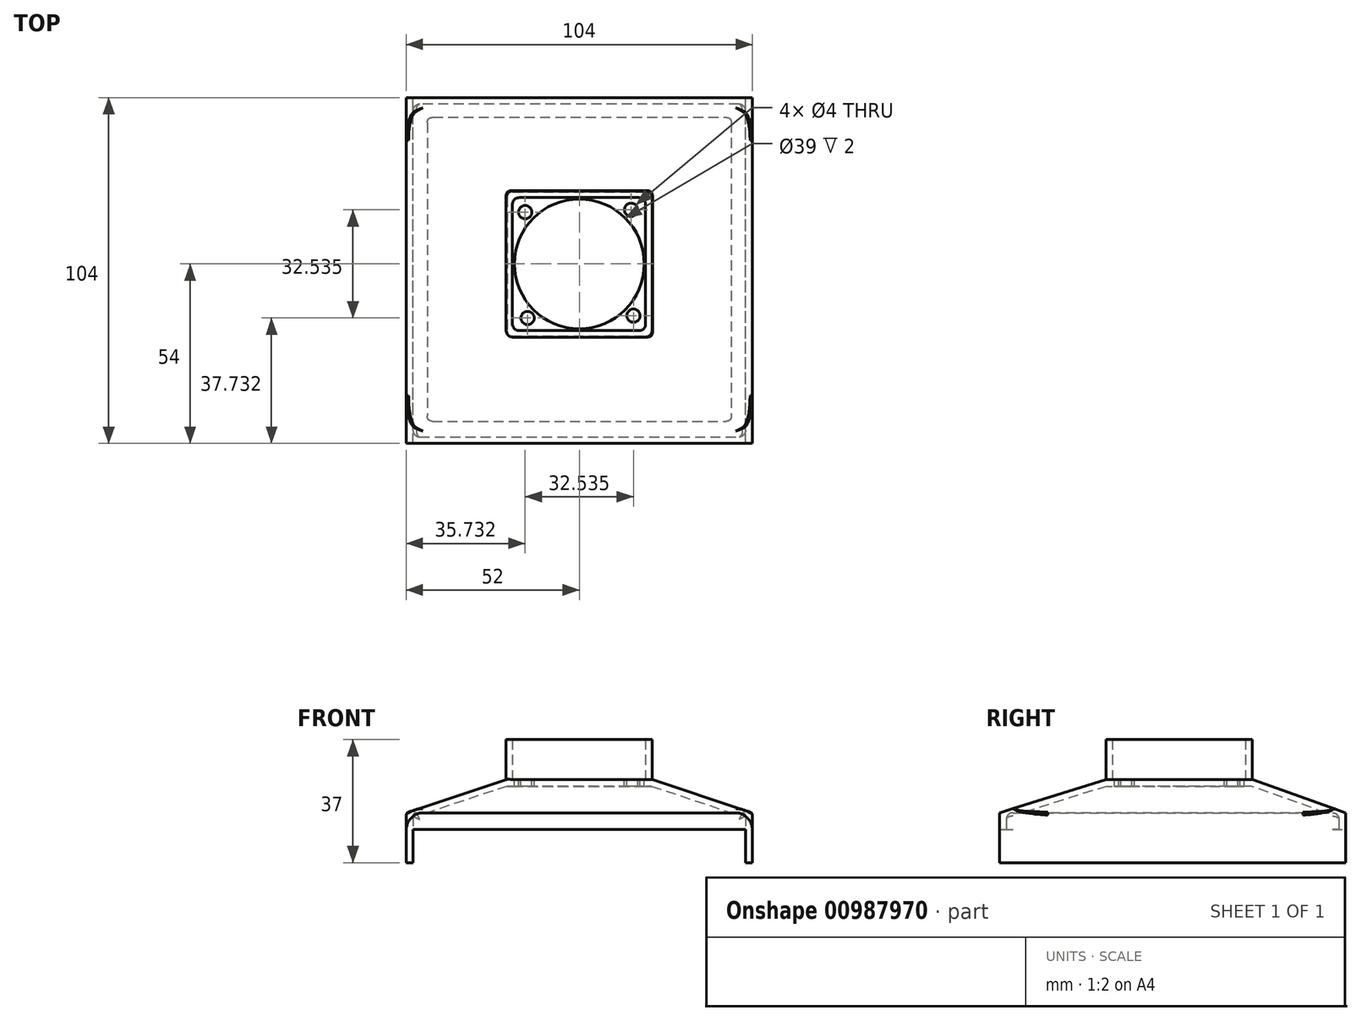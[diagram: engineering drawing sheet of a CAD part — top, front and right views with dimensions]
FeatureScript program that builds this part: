
annotation { "Feature Type Name" : "Feature", "Feature Type Description" : "" }
export const myFeature = defineFeature(function(context is Context, id is Id, definition is map)
    precondition{}
    {
        {
            var Q0;
            Q0=qCreatedBy(makeId("Top.planeOp"),FACE);
            var sketch = newSketch(context, id + "F0", { "sketchPlane" : qUnion([Q0])});
            skLineSegment(sketch, "E0.bottom", {"start": v(-52, 50) * mm, "end": v(52, 50) * mm});
            skLineSegment(sketch, "E0.top", {"start": v(-52, -54) * mm, "end": v(52, -54) * mm});
            skLineSegment(sketch, "E0.left", {"start": v(-52, 50) * mm, "end": v(-52, -54) * mm});
            skLineSegment(sketch, "E0.right", {"start": v(52, 50) * mm, "end": v(52, -54) * mm});
            skSolve(sketch);
        }
        {
            var Q0;
            Q0=qCreatedBy(makeId("Top.planeOp"),FACE);
            cPlane(context, id + "F1", {"entities" : qUnion([Q0]), "cplaneType" : CPlaneType.OFFSET, "offset" : 10 * mm, "width" : 150 * mm, "height" : 150 * mm});
        }
        {
            var Q0;
            Q0=qCreatedBy(id+"F1.planeOp",FACE);
            var sketch = newSketch(context, id + "F2", { "sketchPlane" : qUnion([Q0])});
            skLineSegment(sketch, "E1.bottom", {"start": v(-22, 22) * mm, "end": v(22, 22) * mm});
            skLineSegment(sketch, "E1.top", {"start": v(-22, -22) * mm, "end": v(22, -22) * mm});
            skLineSegment(sketch, "E1.left", {"start": v(-22, 22) * mm, "end": v(-22, -22) * mm});
            skLineSegment(sketch, "E1.right", {"start": v(22, 22) * mm, "end": v(22, -22) * mm});
            skSolve(sketch);
        }
        {
            var Q0;
            Q0=makeQuery(id+"F0.imprint","IMPRINT",FACE,{"disambiguationData":[TD([[makeQuery(id+"F0.imprint","IMPRINT",EDGE,{"derivedFrom":sQuery(id+"F0.wireOp",EDGE,"E0.bottom")}),-1.0]])]});
            var Q1;
            Q1=makeQuery(id+"F2.imprint","IMPRINT",FACE,{"disambiguationData":[TD([[makeQuery(id+"F2.imprint","IMPRINT",EDGE,{"derivedFrom":sQuery(id+"F2.wireOp",EDGE,"E1.bottom")}),-1.0]])]});
            loft(context, id + "F3", {"sheetProfilesArray" : [{ "sheetProfileEntities" : qUnion([Q0]) }, { "sheetProfileEntities" : qUnion([Q1]) }]});
        }
        {
            var Q0;
            Q0=makeQuery(id+"F3.opLoft","CAP_FACE",FACE,{"disambiguationData":[OSD([makeQuery(id+"F0.imprint","IMPRINT",FACE,{"disambiguationData":[TD([[makeQuery(id+"F0.imprint","IMPRINT",EDGE,{"derivedFrom":sQuery(id+"F0.wireOp",EDGE,"E0.bottom")}),-1.0]])]})])],"isStart":true});
            shell(context, id + "F4", {"entities" : qUnion([Q0]), "thickness" : 2 * mm});
        }
        {
            var Q0;
            Q0=makeQuery(id+"F0.imprint","IMPRINT",FACE,{"disambiguationData":[TD([[makeQuery(id+"F0.imprint","IMPRINT",EDGE,{"derivedFrom":sQuery(id+"F0.wireOp",EDGE,"E0.bottom")}),-1.0]])]});
            var sketch = newSketch(context, id + "F5", { "sketchPlane" : qUnion([Q0])});
            skLineSegment(sketch, "E2.0.0", {"start": v(-52, 50) * mm, "end": v(-52, -54) * mm});
            skLineSegment(sketch, "E2.0.1", {"start": v(-52, -54) * mm, "end": v(52, -54) * mm});
            skLineSegment(sketch, "E2.0.2", {"start": v(52, -54) * mm, "end": v(52, 50) * mm});
            skLineSegment(sketch, "E2.0.3", {"start": v(52, 50) * mm, "end": v(-52, 50) * mm});
            skSolve(sketch);
        }
        {
            var Q0;
            Q0=makeQuery(id+"F0.imprint","IMPRINT",FACE,{"disambiguationData":[TD([[makeQuery(id+"F0.imprint","IMPRINT",EDGE,{"derivedFrom":sQuery(id+"F0.wireOp",EDGE,"E0.bottom")}),-1.0]])]});
            extrude(context, id + "F6", {"entities" : qUnion([Q0]), "operationType" : NewBodyOperationType.ADD, "oppositeDirection" : true, "depth" : 15 * mm, "offsetDistance" : 25 * mm});
        }
        {
            var Q0;
            Q0=makeQuery(id+"F6.opExtrude","CAP_FACE",FACE,{"disambiguationData":[OSD([sQuery(id+"F0.wireOp",EDGE,"E0.bottom"),sQuery(id+"F0.wireOp",EDGE,"E0.top"),sQuery(id+"F0.wireOp",EDGE,"E0.left"),sQuery(id+"F0.wireOp",EDGE,"E0.right")])],"isStart":false});
            var sketch = newSketch(context, id + "F7", { "sketchPlane" : qUnion([Q0])});
            skLineSegment(sketch, "E3.bottom", {"start": v(-50, 52) * mm, "end": v(50, 52) * mm});
            skLineSegment(sketch, "E3.top", {"start": v(-50, -48) * mm, "end": v(50, -48) * mm});
            skLineSegment(sketch, "E3.left", {"start": v(-50, 52) * mm, "end": v(-50, -48) * mm});
            skLineSegment(sketch, "E3.right", {"start": v(50, 52) * mm, "end": v(50, -48) * mm});
            skSolve(sketch);
        }
        {
            var Q0;
            Q0=makeQuery(id+"F7.imprint","IMPRINT",FACE,{"disambiguationData":[TD([[makeQuery(id+"F7.imprint","IMPRINT",EDGE,{"derivedFrom":sQuery(id+"F7.wireOp",EDGE,"E3.bottom")}),-1.0]])]});
            extrude(context, id + "F8", {"entities" : qUnion([Q0]), "operationType" : NewBodyOperationType.REMOVE, "oppositeDirection" : true, "depth" : 15 * mm, "offsetDistance" : 25 * mm});
        }
        {
            var Q0;
            Q0=makeQuery(id+"F2.imprint","IMPRINT",FACE,{"disambiguationData":[TD([[makeQuery(id+"F2.imprint","IMPRINT",EDGE,{"derivedFrom":sQuery(id+"F2.wireOp",EDGE,"E1.bottom")}),-1.0]])]});
            var sketch = newSketch(context, id + "F9", { "sketchPlane" : qUnion([Q0])});
            skLineSegment(sketch, "E4.bottom", {"start": v(-20.08, -20.08) * mm, "end": v(19.92, -20.08) * mm});
            skLineSegment(sketch, "E4.top", {"start": v(-20.08, 19.92) * mm, "end": v(19.92, 19.92) * mm});
            skLineSegment(sketch, "E4.left", {"start": v(-20.08, -20.08) * mm, "end": v(-20.08, 19.92) * mm});
            skLineSegment(sketch, "E4.right", {"start": v(19.92, -20.08) * mm, "end": v(19.92, 19.92) * mm});
            skLineSegment(sketch, "E5.0", {"start": v(-22.08, -22.08) * mm, "end": v(-22.08, 21.92) * mm});
            skLineSegment(sketch, "E5.1", {"start": v(-22.08, -22.08) * mm, "end": v(21.92, -22.08) * mm});
            skLineSegment(sketch, "E5.2", {"start": v(21.92, -22.08) * mm, "end": v(21.92, 21.92) * mm});
            skLineSegment(sketch, "E5.3", {"start": v(-22.08, 21.92) * mm, "end": v(21.92, 21.92) * mm});
            skLineSegment(sketch, "E6.0", {"start": v(-27, 22) * mm, "end": v(-27, -22) * mm});
            skSolve(sketch);
        }
        {
            var Q0;
            Q0=makeQuery(id+"F9.imprint","IMPRINT",FACE,{"disambiguationData":[TD([[makeQuery(id+"F9.imprint","IMPRINT",EDGE,{"derivedFrom":sQuery(id+"F9.wireOp",EDGE,"E4.bottom")}),-1.0]])]});
            extrude(context, id + "F10", {"entities" : qUnion([Q0]), "operationType" : NewBodyOperationType.ADD, "depth" : 12 * mm, "offsetDistance" : 25 * mm});
        }
        {
            var Q0;
            Q0=makeQuery(id+"F2.imprint","IMPRINT",FACE,{"disambiguationData":[TD([[makeQuery(id+"F2.imprint","IMPRINT",EDGE,{"derivedFrom":sQuery(id+"F2.wireOp",EDGE,"E1.bottom")}),-1.0]])]});
            var sketch = newSketch(context, id + "F11", { "sketchPlane" : qUnion([Q0])});
            skCircle(sketch, "E7", {"center": v(0, 0) * mm, "radius": 19.5 * mm});
            skCircle(sketch, "E8", {"center": v(16.27, -15.55) * mm, "radius": 2 * mm});
            skCircle(sketch, "E9.1.0", {"center": v(15.55, 16.27) * mm, "radius": 2 * mm});
            skCircle(sketch, "E9.2.0", {"center": v(-16.27, 15.55) * mm, "radius": 2 * mm});
            skCircle(sketch, "E9.3.0", {"center": v(-15.55, -16.27) * mm, "radius": 2 * mm});
            skSolve(sketch);
        }
        {
            var Q0;
            Q0=makeQuery(id+"F11.imprint","IMPRINT",FACE,{"disambiguationData":[TD([[makeQuery(id+"F11.imprint","IMPRINT",EDGE,{"derivedFrom":sQuery(id+"F11.wireOp",EDGE,"E7")}),1.0]])]});
            var Q1;
            Q1=makeQuery(id+"F11.imprint","IMPRINT",FACE,{"disambiguationData":[TD([[makeQuery(id+"F11.imprint","IMPRINT",EDGE,{"derivedFrom":sQuery(id+"F11.wireOp",EDGE,"E8")}),1.0]])]});
            var Q2;
            Q2=makeQuery(id+"F11.imprint","IMPRINT",FACE,{"disambiguationData":[TD([[makeQuery(id+"F11.imprint","IMPRINT",EDGE,{"derivedFrom":sQuery(id+"F11.wireOp",EDGE,"E9.3.0")}),1.0]])]});
            var Q3;
            Q3=makeQuery(id+"F11.imprint","IMPRINT",FACE,{"disambiguationData":[TD([[makeQuery(id+"F11.imprint","IMPRINT",EDGE,{"derivedFrom":sQuery(id+"F11.wireOp",EDGE,"E9.2.0")}),1.0]])]});
            var Q4;
            Q4=makeQuery(id+"F11.imprint","IMPRINT",FACE,{"disambiguationData":[TD([[makeQuery(id+"F11.imprint","IMPRINT",EDGE,{"derivedFrom":sQuery(id+"F11.wireOp",EDGE,"E9.1.0")}),1.0]])]});
            extrude(context, id + "F12", {"entities" : qUnion([Q0, Q1, Q2, Q3, Q4]), "operationType" : NewBodyOperationType.REMOVE, "oppositeDirection" : true, "depth" : 25 * mm, "offsetDistance" : 25 * mm});
        }
        {
            var Q0;
            Q0=makeQuery(id+"F6.opExtrude","SWEPT_FACE",FACE,{"disambiguationData":[OSD([sQuery(id+"F0.wireOp",EDGE,"E0.bottom")])]});
            var sketch = newSketch(context, id + "F13", { "sketchPlane" : qUnion([Q0])});
            skLineSegment(sketch, "E10.bottom", {"start": v(-50, -15) * mm, "end": v(50, -15) * mm});
            skLineSegment(sketch, "E10.top", {"start": v(-50, -5) * mm, "end": v(50, -5) * mm});
            skLineSegment(sketch, "E10.left", {"start": v(-50, -15) * mm, "end": v(-50, -5) * mm});
            skLineSegment(sketch, "E10.right", {"start": v(50, -15) * mm, "end": v(50, -5) * mm});
            skSolve(sketch);
        }
        {
            var Q0;
            Q0=makeQuery(id+"F13.imprint","IMPRINT",FACE,{"disambiguationData":[TD([[makeQuery(id+"F13.imprint","IMPRINT",EDGE,{"derivedFrom":sQuery(id+"F13.wireOp",EDGE,"E10.bottom")}),-1.0]])]});
            extrude(context, id + "F14", {"entities" : qUnion([Q0]), "operationType" : NewBodyOperationType.REMOVE, "oppositeDirection" : true, "depth" : 125 * mm, "offsetDistance" : 25 * mm});
        }
        {
            var Q0;
            Q0=makeQuery(id+"F10.opExtrude","SWEPT_EDGE",EDGE,{"disambiguationData":[OSD([sQuery(id+"F2.wireOp",EDGE,"E1.left"),sQuery(id+"F9.wireOp",EDGE,"E5.3")])]});
            var Q1;
            Q1=makeQuery(id+"F10.opExtrude","SWEPT_EDGE",EDGE,{"disambiguationData":[OSD([sQuery(id+"F2.wireOp",EDGE,"E1.top"),sQuery(id+"F2.wireOp",EDGE,"E1.left")])]});
            var Q2;
            Q2=makeQuery(id+"F10.opExtrude","SWEPT_EDGE",EDGE,{"disambiguationData":[OSD([sQuery(id+"F2.wireOp",EDGE,"E1.top"),sQuery(id+"F9.wireOp",EDGE,"E5.2")])]});
            var Q3;
            Q3=makeQuery(id+"F10.opExtrude","SWEPT_EDGE",EDGE,{"disambiguationData":[OSD([sQuery(id+"F9.wireOp",EDGE,"E5.2"),sQuery(id+"F9.wireOp",EDGE,"E5.3")])]});
            var Q4;
            Q4=makeQuery(id+"F10.opExtrude","SWEPT_EDGE",EDGE,{"disambiguationData":[OSD([sQuery(id+"F9.wireOp",EDGE,"E4.top"),sQuery(id+"F9.wireOp",EDGE,"E4.right")])]});
            var Q5;
            Q5=makeQuery(id+"F10.opExtrude","SWEPT_EDGE",EDGE,{"disambiguationData":[OSD([sQuery(id+"F9.wireOp",EDGE,"E4.bottom"),sQuery(id+"F9.wireOp",EDGE,"E4.right")])]});
            var Q6;
            Q6=makeQuery(id+"F10.opExtrude","SWEPT_EDGE",EDGE,{"disambiguationData":[OSD([sQuery(id+"F9.wireOp",EDGE,"E4.bottom"),sQuery(id+"F9.wireOp",EDGE,"E4.left")])]});
            var Q7;
            Q7=makeQuery(id+"F10.opExtrude","SWEPT_EDGE",EDGE,{"disambiguationData":[OSD([sQuery(id+"F9.wireOp",EDGE,"E4.top"),sQuery(id+"F9.wireOp",EDGE,"E4.left")])]});
            fillet(context, id + "F15", {"entities" : qUnion([Q0, Q1, Q2, Q3, Q4, Q5, Q6, Q7]), "radius" : 2 * mm, "tangentPropagation" : true, "allowEdgeOverflow" : false});
        }
        {
            var Q0;
            {var subQ0=sQuery(id+"F0.wireOp",EDGE,"E0.left");Q0=makeQuery(id+"F6.boolean.opBoolean","MERGE",EDGE,{"derivedFrom":[makeQuery(id+"F3.opLoft","MID_CAP_EDGE",EDGE,{"disambiguationData":[OSD([sQuery(id+"F0.wireOp",EDGE,"E0.bottom"),sQuery(id+"F0.wireOp",EDGE,"E0.top"),subQ0])],"capPos":0.0}),makeQuery(id+"F6.opExtrude","CAP_EDGE",EDGE,{"disambiguationData":[OSD([subQ0])],"isStart":true})]});}
            var Q1;
            {var subQ0=sQuery(id+"F0.wireOp",EDGE,"E0.right");Q1=makeQuery(id+"F6.boolean.opBoolean","MERGE",EDGE,{"derivedFrom":[makeQuery(id+"F3.opLoft","MID_CAP_EDGE",EDGE,{"disambiguationData":[OSD([sQuery(id+"F0.wireOp",EDGE,"E0.bottom"),sQuery(id+"F0.wireOp",EDGE,"E0.top"),subQ0])],"capPos":0.0}),makeQuery(id+"F6.opExtrude","CAP_EDGE",EDGE,{"disambiguationData":[OSD([subQ0])],"isStart":true})]});}
            var Q2;
            Q2=makeQuery(id+"F8.boolean.opBoolean","COPY",EDGE,{"derivedFrom":makeQuery(id+"F8.opExtrude","CAP_EDGE",EDGE,{"disambiguationData":[OSD([sQuery(id+"F7.wireOp",EDGE,"E3.right")])],"isStart":false})});
            var Q3;
            Q3=makeQuery(id+"F8.boolean.opBoolean","COPY",EDGE,{"derivedFrom":makeQuery(id+"F8.opExtrude","CAP_EDGE",EDGE,{"disambiguationData":[OSD([sQuery(id+"F7.wireOp",EDGE,"E3.left")])],"isStart":false})});
            fillet(context, id + "F16", {"entities" : qUnion([Q0, Q1, Q2, Q3]), "radius" : 1 * mm, "tangentPropagation" : true, "allowEdgeOverflow" : false});
        }
        {
            var Q0;
            Q0=makeQuery(id+"F3.opLoft","SWEPT_EDGE",EDGE,{"disambiguationData":[OSD([sQuery(id+"F0.wireOp",EDGE,"E0.top"),sQuery(id+"F0.wireOp",EDGE,"E0.left"),sQuery(id+"F2.wireOp",EDGE,"E1.top"),sQuery(id+"F2.wireOp",EDGE,"E1.left")])]});
            var Q1;
            Q1=makeQuery(id+"F3.opLoft","SWEPT_EDGE",EDGE,{"disambiguationData":[OSD([sQuery(id+"F0.wireOp",EDGE,"E0.top"),sQuery(id+"F0.wireOp",EDGE,"E0.right"),sQuery(id+"F2.wireOp",EDGE,"E1.top"),sQuery(id+"F2.wireOp",EDGE,"E1.right")])]});
            var Q2;
            Q2=makeQuery(id+"F3.opLoft","SWEPT_EDGE",EDGE,{"disambiguationData":[OSD([sQuery(id+"F0.wireOp",EDGE,"E0.bottom"),sQuery(id+"F0.wireOp",EDGE,"E0.left"),sQuery(id+"F2.wireOp",EDGE,"E1.bottom"),sQuery(id+"F2.wireOp",EDGE,"E1.left")])]});
            var Q3;
            Q3=makeQuery(id+"F3.opLoft","SWEPT_EDGE",EDGE,{"disambiguationData":[OSD([sQuery(id+"F0.wireOp",EDGE,"E0.bottom"),sQuery(id+"F0.wireOp",EDGE,"E0.right"),sQuery(id+"F2.wireOp",EDGE,"E1.bottom"),sQuery(id+"F2.wireOp",EDGE,"E1.right")])]});
            var Q4;
            Q4=makeQuery(id+"F4.opShell","OFFSET_EDGE",EDGE,{"disambiguationData":[OSD([sQuery(id+"F0.wireOp",EDGE,"E0.top"),sQuery(id+"F0.wireOp",EDGE,"E0.left"),sQuery(id+"F2.wireOp",EDGE,"E1.top"),sQuery(id+"F2.wireOp",EDGE,"E1.left")])]});
            var Q5;
            Q5=makeQuery(id+"F4.opShell","OFFSET_EDGE",EDGE,{"disambiguationData":[OSD([sQuery(id+"F0.wireOp",EDGE,"E0.top"),sQuery(id+"F0.wireOp",EDGE,"E0.right"),sQuery(id+"F2.wireOp",EDGE,"E1.top"),sQuery(id+"F2.wireOp",EDGE,"E1.right")])]});
            var Q6;
            Q6=makeQuery(id+"F4.opShell","OFFSET_EDGE",EDGE,{"disambiguationData":[OSD([sQuery(id+"F0.wireOp",EDGE,"E0.bottom"),sQuery(id+"F0.wireOp",EDGE,"E0.right"),sQuery(id+"F2.wireOp",EDGE,"E1.bottom"),sQuery(id+"F2.wireOp",EDGE,"E1.right")])]});
            var Q7;
            Q7=makeQuery(id+"F4.opShell","OFFSET_EDGE",EDGE,{"disambiguationData":[OSD([sQuery(id+"F0.wireOp",EDGE,"E0.bottom"),sQuery(id+"F0.wireOp",EDGE,"E0.left"),sQuery(id+"F2.wireOp",EDGE,"E1.bottom"),sQuery(id+"F2.wireOp",EDGE,"E1.left")])]});
            fillet(context, id + "F17", {"entities" : qUnion([Q0, Q1, Q2, Q3, Q4, Q5, Q6, Q7]), "radius" : 5 * mm, "tangentPropagation" : true, "allowEdgeOverflow" : false});
        }
        {
            var Q0;
            Q0=makeQuery(id+"F8.boolean.opBoolean","COPY",EDGE,{"derivedFrom":makeQuery(id+"F8.opExtrude","SWEPT_EDGE",EDGE,{"disambiguationData":[OSD([sQuery(id+"F7.wireOp",EDGE,"E3.top"),sQuery(id+"F7.wireOp",EDGE,"E3.left")])]})});
            var Q1;
            Q1=makeQuery(id+"F8.boolean.opBoolean","COPY",EDGE,{"derivedFrom":makeQuery(id+"F8.opExtrude","SWEPT_EDGE",EDGE,{"disambiguationData":[OSD([sQuery(id+"F7.wireOp",EDGE,"E3.bottom"),sQuery(id+"F7.wireOp",EDGE,"E3.left")])]})});
            fillet(context, id + "F18", {"entities" : qUnion([Q0, Q1]), "radius" : 2 * mm, "tangentPropagation" : true, "allowEdgeOverflow" : false});
        }
    });
